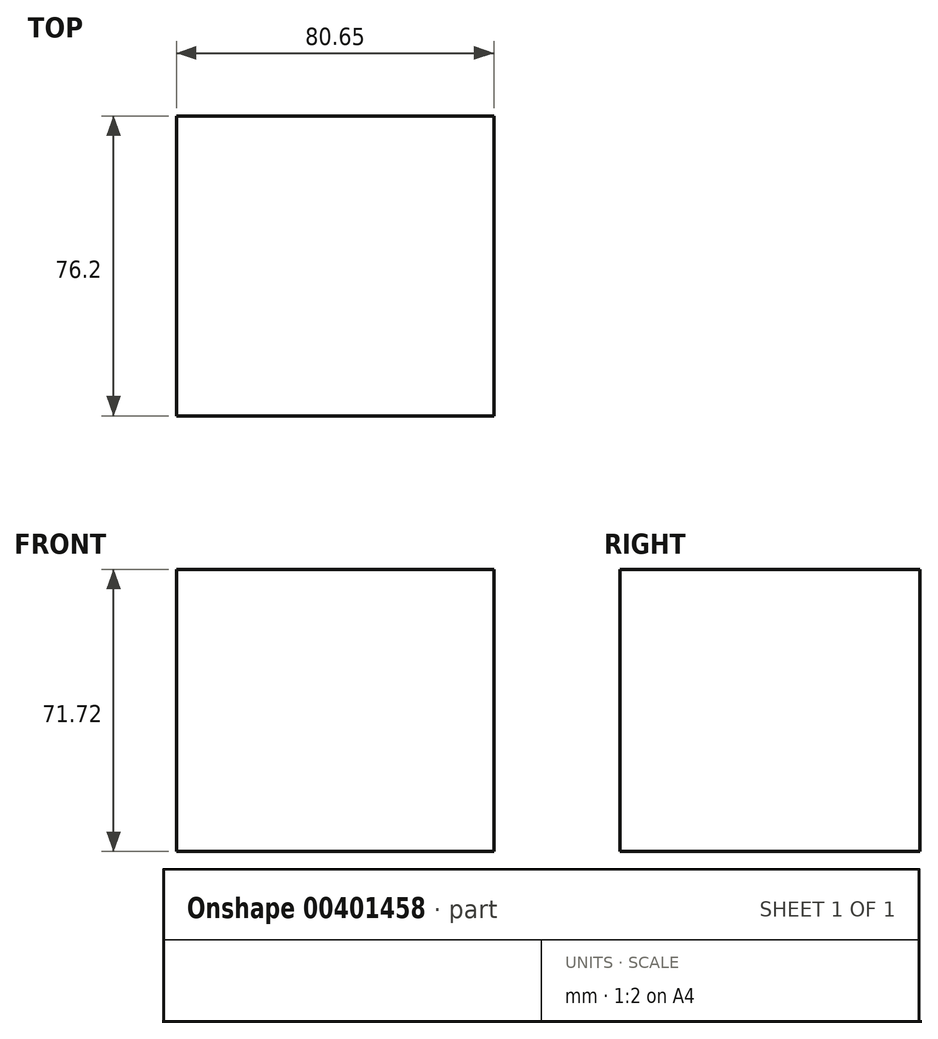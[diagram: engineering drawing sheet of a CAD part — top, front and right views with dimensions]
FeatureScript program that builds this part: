
annotation { "Feature Type Name" : "Feature", "Feature Type Description" : "" }
export const myFeature = defineFeature(function(context is Context, id is Id, definition is map)
    precondition{}
    {
        {
            var Q0;
            Q0=qCreatedBy(makeId("Front.planeOp"),FACE);
            var sketch = newSketch(context, id + "F0", { "sketchPlane" : qUnion([Q0])});
            skLineSegment(sketch, "E0.bottom", {"start": v(0, 0) * mm, "end": v(80.65, 0) * mm});
            skLineSegment(sketch, "E0.top", {"start": v(0, 71.72) * mm, "end": v(80.65, 71.72) * mm});
            skLineSegment(sketch, "E0.left", {"start": v(0, 0) * mm, "end": v(0, 71.72) * mm});
            skLineSegment(sketch, "E0.right", {"start": v(80.65, 0) * mm, "end": v(80.65, 71.72) * mm});
            skSolve(sketch);
        }
        {
            var Q0;
            Q0 = qSketchRegion(id + "F0", true);
            extrude(context, id + "F1", {"entities" : qUnion([Q0]), "depth" : 76.2 * mm});
        }
    });
